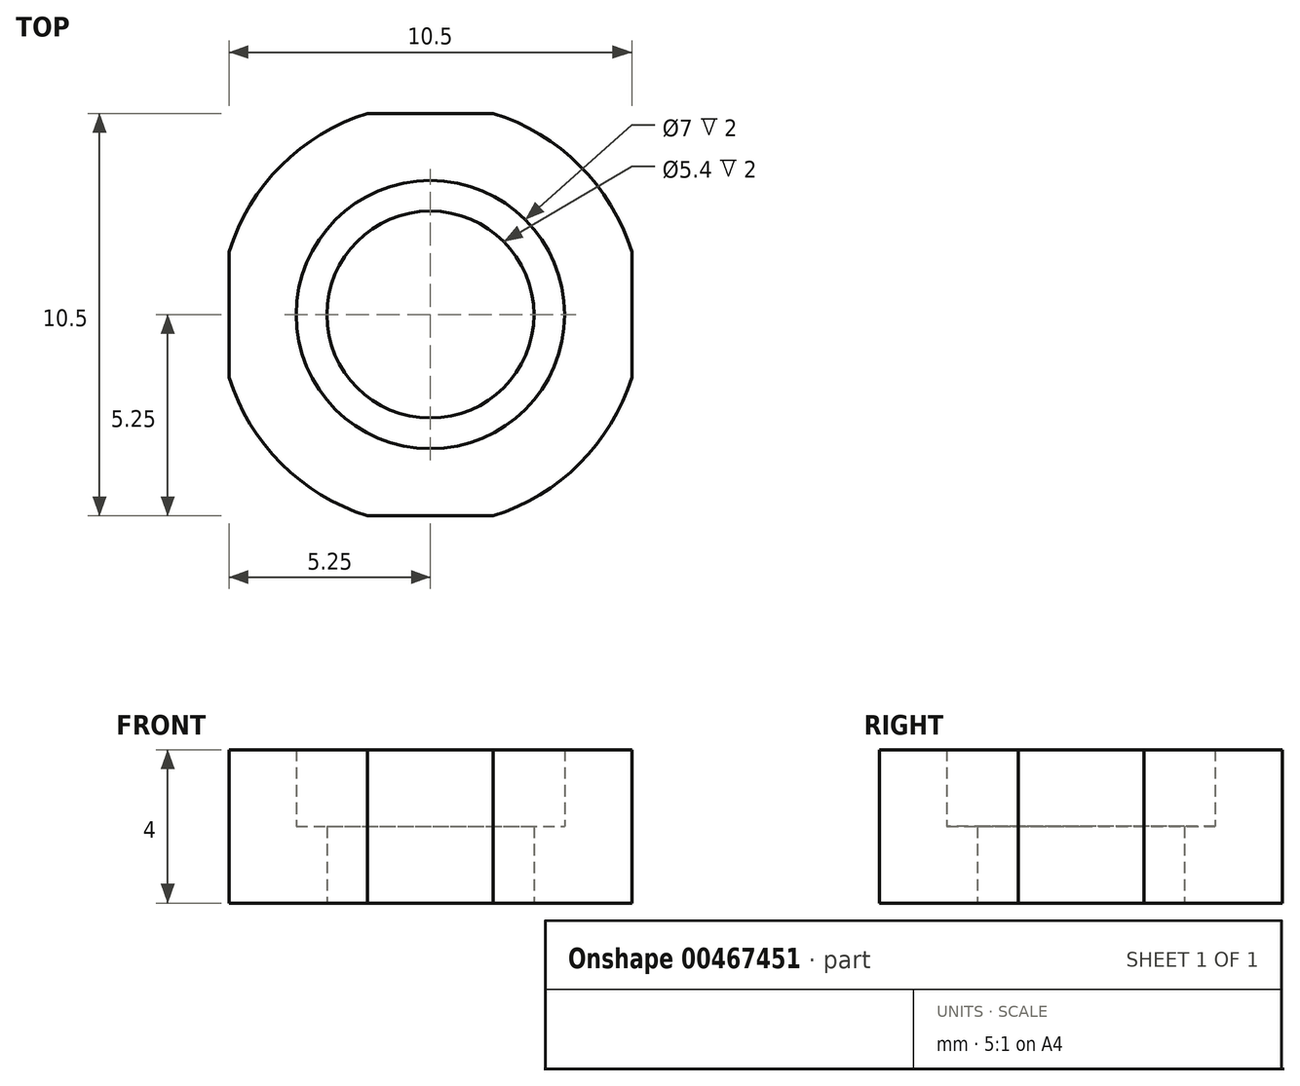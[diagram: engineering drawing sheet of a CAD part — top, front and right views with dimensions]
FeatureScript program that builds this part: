
annotation { "Feature Type Name" : "Feature", "Feature Type Description" : "" }
export const myFeature = defineFeature(function(context is Context, id is Id, definition is map)
    precondition{}
    {
        {
            var Q0;
            Q0=qCreatedBy(makeId("Front.planeOp"),FACE);
            var sketch = newSketch(context, id + "F0", { "sketchPlane" : qUnion([Q0])});
            skLineSegment(sketch, "E0", {"start": v(3.5, 4) * mm, "end": v(3.5, 2) * mm});
            skLineSegment(sketch, "E1", {"start": v(3.5, 2) * mm, "end": v(2.7, 2) * mm});
            skLineSegment(sketch, "E2", {"start": v(2.7, 2) * mm, "end": v(2.7, 0) * mm});
            skLineSegment(sketch, "E3", {"start": v(2.7, 0) * mm, "end": v(5.5, 0) * mm});
            skLineSegment(sketch, "E4", {"start": v(5.5, 0) * mm, "end": v(5.5, 4) * mm});
            skLineSegment(sketch, "E5", {"start": v(5.5, 4) * mm, "end": v(3.5, 4) * mm});
            skLineSegment(sketch, "E6", {"start": v(0, 0) * mm, "end": v(0, 11.76) * mm, "construction": true});
            skSolve(sketch);
        }
        {
            var Q0;
            Q0=makeQuery(id+"F0.imprint","IMPRINT",FACE,{"disambiguationData":[TD([[makeQuery(id+"F0.imprint","IMPRINT",EDGE,{"derivedFrom":sQuery(id+"F0.wireOp",EDGE,"E0")}),1.0]])]});
            var Q1;
            Q1=sQuery(id+"F0.wireOp",EDGE,"E6");
            revolve(context, id + "F1", {"entities" : qUnion([Q0]), "axis" : qUnion([Q1]), "revolveType" : RevolveType.FULL});
        }
        {
            var Q0;
            Q0=qCreatedBy(makeId("Top.planeOp"),FACE);
            var sketch = newSketch(context, id + "F2", { "sketchPlane" : qUnion([Q0])});
            skLineSegment(sketch, "E7.bottom", {"start": v(-5.25, 5.25) * mm, "end": v(5.25, 5.25) * mm});
            skLineSegment(sketch, "E7.top", {"start": v(-5.25, -5.25) * mm, "end": v(5.25, -5.25) * mm});
            skLineSegment(sketch, "E7.left", {"start": v(-5.25, 5.25) * mm, "end": v(-5.25, -5.25) * mm});
            skLineSegment(sketch, "E7.right", {"start": v(5.25, 5.25) * mm, "end": v(5.25, -5.25) * mm});
            skLineSegment(sketch, "E8", {"start": v(-5.25, 0) * mm, "end": v(5.25, 0) * mm, "construction": true});
            skLineSegment(sketch, "E9", {"start": v(0, 5.25) * mm, "end": v(0, -5.25) * mm, "construction": true});
            skPoint(sketch, "E10", {"position": v(0, 0) * mm});
            skLineSegment(sketch, "E11.0", {"start": v(-5.75, 5.75) * mm, "end": v(5.75, 5.75) * mm});
            skLineSegment(sketch, "E11.1", {"start": v(-5.75, 5.75) * mm, "end": v(-5.75, -5.75) * mm});
            skLineSegment(sketch, "E11.2", {"start": v(-5.75, -5.75) * mm, "end": v(5.75, -5.75) * mm});
            skLineSegment(sketch, "E11.3", {"start": v(5.75, 5.75) * mm, "end": v(5.75, -5.75) * mm});
            skSolve(sketch);
        }
        {
            var Q0;
            Q0=makeQuery(id+"F2.imprint","IMPRINT",FACE,{"disambiguationData":[TD([[makeQuery(id+"F2.imprint","IMPRINT",EDGE,{"derivedFrom":sQuery(id+"F2.wireOp",EDGE,"E7.bottom")}),1.0]])]});
            extrude(context, id + "F3", {"entities" : qUnion([Q0]), "operationType" : NewBodyOperationType.REMOVE, "depth" : 25 * mm});
        }
    });
